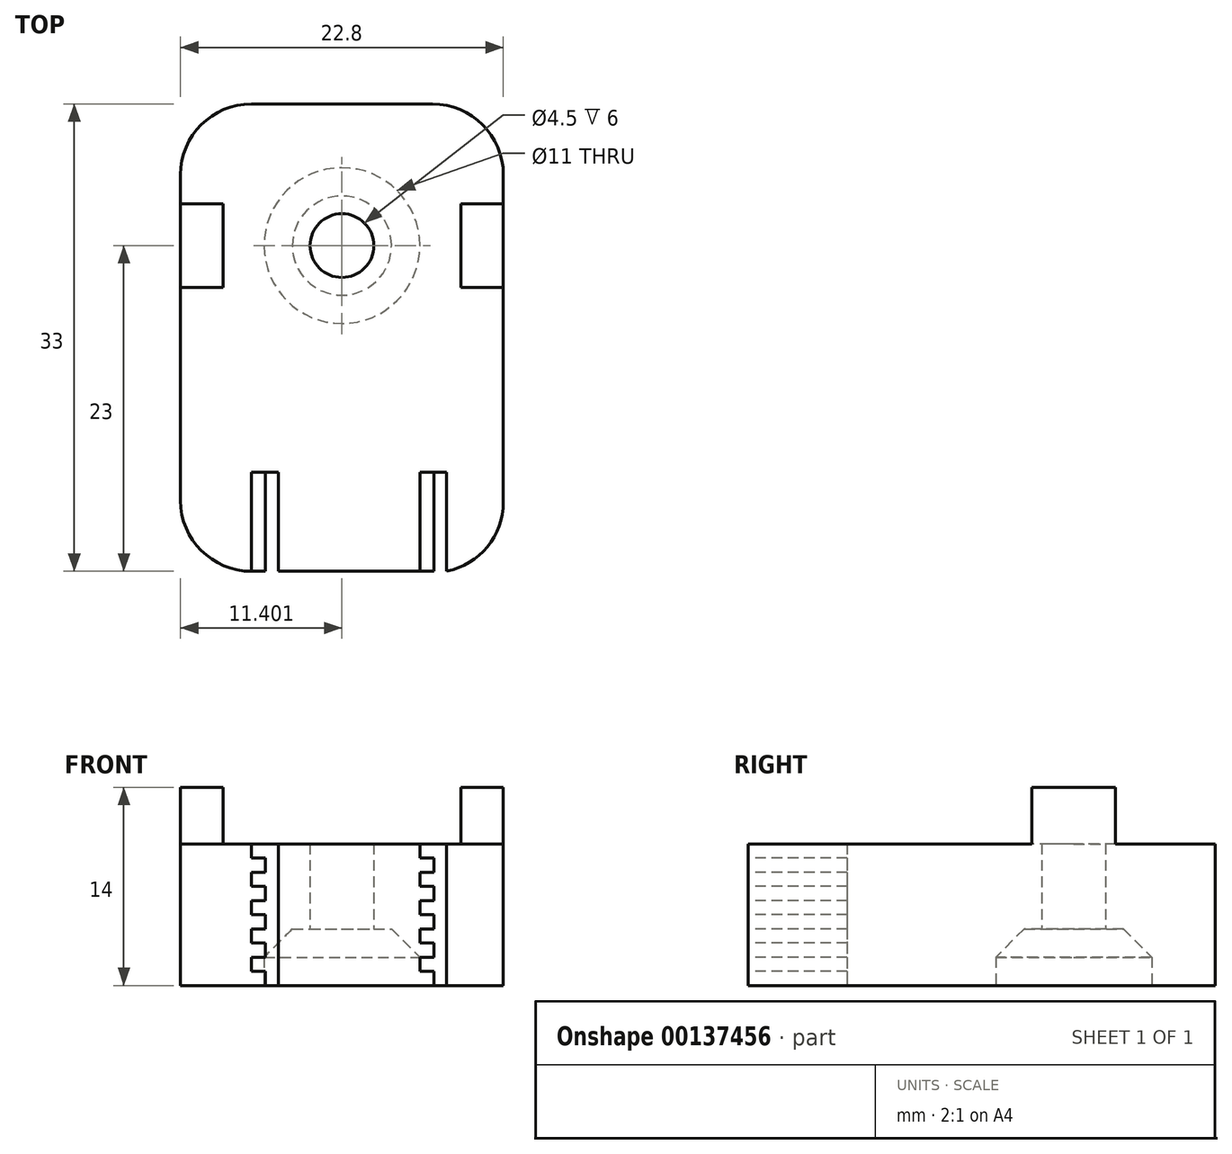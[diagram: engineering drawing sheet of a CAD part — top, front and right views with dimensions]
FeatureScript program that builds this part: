
annotation { "Feature Type Name" : "Feature", "Feature Type Description" : "" }
export const myFeature = defineFeature(function(context is Context, id is Id, definition is map)
    precondition{}
    {
        {
            var Q0;
            Q0=qCreatedBy(makeId("Top.planeOp"),FACE);
            var sketch = newSketch(context, id + "F0", { "sketchPlane" : qUnion([Q0])});
            skLineSegment(sketch, "E0.bottom", {"start": v(-4.06, 0) * mm, "end": v(14.44, 0) * mm});
            skLineSegment(sketch, "E0.top", {"start": v(-4.06, 33) * mm, "end": v(14.44, 33) * mm});
            skLineSegment(sketch, "E0.left", {"start": v(-4.06, 0) * mm, "end": v(-4.06, 33) * mm});
            skLineSegment(sketch, "E0.right", {"start": v(14.44, 0) * mm, "end": v(14.44, 33) * mm});
            skLineSegment(sketch, "E1", {"start": v(-4.06, 13) * mm, "end": v(14.44, 13) * mm});
            skLineSegment(sketch, "E2.bottom", {"start": v(-4.06, 25.95) * mm, "end": v(-1.06, 25.95) * mm});
            skLineSegment(sketch, "E2.top", {"start": v(-4.06, 20.05) * mm, "end": v(-1.06, 20.05) * mm});
            skLineSegment(sketch, "E2.left", {"start": v(-4.06, 25.95) * mm, "end": v(-4.06, 20.05) * mm});
            skLineSegment(sketch, "E2.right", {"start": v(-1.06, 25.95) * mm, "end": v(-1.06, 20.05) * mm});
            skLineSegment(sketch, "E3.bottom", {"start": v(14.44, 25.95) * mm, "end": v(11.44, 25.95) * mm});
            skLineSegment(sketch, "E3.top", {"start": v(14.44, 20.05) * mm, "end": v(11.44, 20.05) * mm});
            skLineSegment(sketch, "E3.left", {"start": v(14.44, 25.95) * mm, "end": v(14.44, 20.05) * mm});
            skLineSegment(sketch, "E3.right", {"start": v(11.44, 25.95) * mm, "end": v(11.44, 20.05) * mm});
            skCircle(sketch, "E4", {"center": v(5.2, 23) * mm, "radius": 2.25 * mm});
            skPoint(sketch, "E5", {"position": v(-1.06, 23) * mm});
            skPoint(sketch, "E6", {"position": v(-4.06, 23) * mm});
            skLineSegment(sketch, "E7", {"start": v(-4.06, 23) * mm, "end": v(14.44, 23) * mm});
            skLineSegment(sketch, "E8.bottom", {"start": v(14.44, 13) * mm, "end": v(18.74, 13) * mm});
            skLineSegment(sketch, "E8.top", {"start": v(14.44, 0) * mm, "end": v(18.74, 0) * mm});
            skLineSegment(sketch, "E8.left", {"start": v(14.44, 13) * mm, "end": v(14.44, 0) * mm});
            skLineSegment(sketch, "E8.right", {"start": v(18.74, 13) * mm, "end": v(18.74, 0) * mm});
            skLineSegment(sketch, "E9.bottom", {"start": v(14.44, 33) * mm, "end": v(18.74, 33) * mm});
            skLineSegment(sketch, "E9.left", {"start": v(14.44, 33) * mm, "end": v(14.44, 13) * mm});
            skLineSegment(sketch, "E9.right", {"start": v(18.74, 33) * mm, "end": v(18.74, 13) * mm});
            skLineSegment(sketch, "E10.bottom", {"start": v(18.74, 25.95) * mm, "end": v(15.74, 25.95) * mm});
            skLineSegment(sketch, "E10.top", {"start": v(18.74, 20.05) * mm, "end": v(15.74, 20.05) * mm});
            skLineSegment(sketch, "E10.left", {"start": v(18.74, 25.95) * mm, "end": v(18.74, 20.05) * mm});
            skLineSegment(sketch, "E10.right", {"start": v(15.74, 25.95) * mm, "end": v(15.74, 20.05) * mm});
            skCircle(sketch, "E11", {"center": v(7.34, 23) * mm, "radius": 2.25 * mm});
            skPoint(sketch, "E12", {"position": v(7.34, 0) * mm});
            skSolve(sketch);
        }
        {
            var Q0;
            {var subQ0=sQuery(id+"F0.wireOp",EDGE,"E0.bottom");Q0=makeQuery(id+"F0.imprint","IMPRINT",FACE,{"disambiguationData":[TD([[makeQuery(id+"F0.imprint","IMPRINT",EDGE,{"derivedFrom":subQ0}),1.0]])]});}
            var Q1;
            Q1=makeQuery(id+"F0.imprint","IMPRINT",FACE,{"disambiguationData":[TD([[makeQuery(id+"F0.imprint","IMPRINT",EDGE,{"derivedFrom":sQuery(id+"F0.wireOp",EDGE,"E8.bottom")}),-1.0]])]});
            var Q2;
            Q2=makeQuery(id+"F0.imprint","IMPRINT",FACE,{"disambiguationData":[TD([[makeQuery(id+"F0.imprint","IMPRINT",EDGE,{"derivedFrom":sQuery(id+"F0.wireOp",EDGE,"E8.top")}),1.0]])]});
            var Q3;
            {var subQ9=sQuery(id+"F0.wireOp",EDGE,"E9.bottom");Q3=makeQuery(id+"F0.imprint","IMPRINT",FACE,{"disambiguationData":[TD([[makeQuery(id+"F0.imprint","IMPRINT",EDGE,{"derivedFrom":subQ9}),-1.0]])]});}
            var Q4;
            {var subQ5=sQuery(id+"F0.wireOp",EDGE,"E1");Q4=makeQuery(id+"F0.imprint","IMPRINT",FACE,{"disambiguationData":[TD([[makeQuery(id+"F0.imprint","IMPRINT",EDGE,{"derivedFrom":subQ5}),1.0]])]});}
            var Q5;
            {var subQ1=sQuery(id+"F0.wireOp",EDGE,"E3.top");Q5=makeQuery(id+"F0.imprint","IMPRINT",FACE,{"disambiguationData":[TD([[makeQuery(id+"F0.imprint","IMPRINT",EDGE,{"derivedFrom":subQ1}),-1.0]])]});}
            var Q6;
            {var subQ6=sQuery(id+"F0.wireOp",EDGE,"E3.bottom");Q6=makeQuery(id+"F0.imprint","IMPRINT",FACE,{"disambiguationData":[TD([[makeQuery(id+"F0.imprint","IMPRINT",EDGE,{"derivedFrom":subQ6}),1.0]])]});}
            var Q7;
            {var subQ5=sQuery(id+"F0.wireOp",EDGE,"E0.top");Q7=makeQuery(id+"F0.imprint","IMPRINT",FACE,{"disambiguationData":[TD([[makeQuery(id+"F0.imprint","IMPRINT",EDGE,{"derivedFrom":subQ5}),-1.0]])]});}
            var Q8;
            {var subQ0=sQuery(id+"F0.wireOp",EDGE,"E7");var subQ1=sQuery(id+"F0.wireOp",EDGE,"E4");var subQ2=makeQuery(id+"F0.imprint","INTERSECT",VERTEX,{"disambiguationData":[OD(1.0)],"derivedFrom":[subQ1,subQ0]});Q8=makeQuery(id+"F0.imprint","IMPRINT",FACE,{"disambiguationData":[TD([[makeQuery(id+"F0.imprint","IMPRINT",EDGE,{"disambiguationData":[TD([[subQ2,-1.0]])],"derivedFrom":subQ1}),1.0]])]});}
            var Q9;
            {var subQ0=sQuery(id+"F0.wireOp",EDGE,"E11");var subQ1=sQuery(id+"F0.wireOp",EDGE,"E4");var subQ2=makeQuery(id+"F0.imprint","INTERSECT",VERTEX,{"disambiguationData":[OD(0.0)],"derivedFrom":[subQ1,subQ0]});Q9=makeQuery(id+"F0.imprint","IMPRINT",FACE,{"disambiguationData":[TD([[makeQuery(id+"F0.imprint","IMPRINT",EDGE,{"disambiguationData":[TD([[subQ2,-1.0]])],"derivedFrom":subQ1}),1.0]])]});}
            extrude(context, id + "F1", {"entities" : qUnion([Q0, Q1, Q2, Q3, Q4, Q5, Q6, Q7, Q8, Q9]), "depth" : 10 * mm});
        }
        {
            var Q0;
            Q0=makeQuery(id+"F1.opExtrude","SWEPT_FACE",FACE,{"disambiguationData":[OSD([sQuery(id+"F0.wireOp",EDGE,"E0.bottom")])]});
            var sketch = newSketch(context, id + "F2", { "sketchPlane" : qUnion([Q0])});
            skLineSegment(sketch, "E13", {"start": v(0.94, 10) * mm, "end": v(0.94, 9) * mm});
            skLineSegment(sketch, "E14", {"start": v(0.94, 9) * mm, "end": v(1.94, 9) * mm});
            skLineSegment(sketch, "E15", {"start": v(1.94, 9) * mm, "end": v(1.94, 8) * mm});
            skLineSegment(sketch, "E16", {"start": v(1.94, 8) * mm, "end": v(0.94, 8) * mm});
            skLineSegment(sketch, "E17", {"start": v(0.94, 8) * mm, "end": v(0.94, 7) * mm});
            skLineSegment(sketch, "E18", {"start": v(0.94, 7) * mm, "end": v(1.94, 7) * mm});
            skLineSegment(sketch, "E19", {"start": v(1.94, 7) * mm, "end": v(1.94, 6) * mm});
            skLineSegment(sketch, "E20", {"start": v(1.94, 6) * mm, "end": v(0.94, 6) * mm});
            skLineSegment(sketch, "E21", {"start": v(0.94, 6) * mm, "end": v(0.94, 5) * mm});
            skLineSegment(sketch, "E22", {"start": v(0.94, 5) * mm, "end": v(1.94, 5) * mm});
            skLineSegment(sketch, "E23", {"start": v(1.94, 5) * mm, "end": v(1.94, 4) * mm});
            skLineSegment(sketch, "E24", {"start": v(1.94, 4) * mm, "end": v(0.94, 4) * mm});
            skLineSegment(sketch, "E25", {"start": v(0.94, 4) * mm, "end": v(0.94, 3) * mm});
            skLineSegment(sketch, "E26", {"start": v(0.94, 3) * mm, "end": v(1.94, 3) * mm});
            skLineSegment(sketch, "E27", {"start": v(1.94, 3) * mm, "end": v(1.94, 2) * mm});
            skLineSegment(sketch, "E28", {"start": v(1.94, 2) * mm, "end": v(0.94, 2) * mm});
            skLineSegment(sketch, "E29", {"start": v(0.94, 2) * mm, "end": v(0.94, 1) * mm});
            skLineSegment(sketch, "E30", {"start": v(0.94, 1) * mm, "end": v(1.94, 1) * mm});
            skLineSegment(sketch, "E31", {"start": v(1.94, 1) * mm, "end": v(1.94, 0) * mm});
            skLineSegment(sketch, "E32", {"start": v(1.94, 0) * mm, "end": v(0.94, 0) * mm});
            skLineSegment(sketch, "E33", {"start": v(2.84, 10) * mm, "end": v(2.84, 0) * mm});
            skLineSegment(sketch, "E34", {"start": v(0.94, 10) * mm, "end": v(2.84, 10) * mm});
            skLineSegment(sketch, "E35", {"start": v(2.84, 0) * mm, "end": v(1.94, 0) * mm});
            skLineSegment(sketch, "E36", {"start": v(12.84, 10) * mm, "end": v(12.84, 9) * mm});
            skLineSegment(sketch, "E37", {"start": v(12.84, 9) * mm, "end": v(13.84, 9) * mm});
            skLineSegment(sketch, "E38", {"start": v(13.84, 9) * mm, "end": v(13.84, 8) * mm});
            skLineSegment(sketch, "E39", {"start": v(13.84, 8) * mm, "end": v(12.84, 8) * mm});
            skLineSegment(sketch, "E40", {"start": v(12.84, 8) * mm, "end": v(12.84, 7) * mm});
            skLineSegment(sketch, "E41", {"start": v(12.84, 7) * mm, "end": v(13.84, 7) * mm});
            skLineSegment(sketch, "E42", {"start": v(13.84, 7) * mm, "end": v(13.84, 6) * mm});
            skLineSegment(sketch, "E43", {"start": v(13.84, 6) * mm, "end": v(12.84, 6) * mm});
            skLineSegment(sketch, "E44", {"start": v(12.84, 6) * mm, "end": v(12.84, 5) * mm});
            skLineSegment(sketch, "E45", {"start": v(12.84, 5) * mm, "end": v(13.84, 5) * mm});
            skLineSegment(sketch, "E46", {"start": v(13.84, 5) * mm, "end": v(13.84, 4) * mm});
            skLineSegment(sketch, "E47", {"start": v(13.84, 4) * mm, "end": v(12.84, 4) * mm});
            skLineSegment(sketch, "E48", {"start": v(12.84, 4) * mm, "end": v(12.84, 3) * mm});
            skLineSegment(sketch, "E49", {"start": v(12.84, 3) * mm, "end": v(13.84, 3) * mm});
            skLineSegment(sketch, "E50", {"start": v(13.84, 3) * mm, "end": v(13.84, 2) * mm});
            skLineSegment(sketch, "E51", {"start": v(13.84, 2) * mm, "end": v(12.84, 2) * mm});
            skLineSegment(sketch, "E52", {"start": v(12.84, 2) * mm, "end": v(12.84, 1) * mm});
            skLineSegment(sketch, "E53", {"start": v(12.84, 1) * mm, "end": v(13.84, 1) * mm});
            skLineSegment(sketch, "E54", {"start": v(13.84, 1) * mm, "end": v(13.84, 0) * mm});
            skLineSegment(sketch, "E55", {"start": v(13.84, 0) * mm, "end": v(12.84, 0) * mm});
            skLineSegment(sketch, "E56", {"start": v(14.74, 10) * mm, "end": v(14.74, 0) * mm});
            skLineSegment(sketch, "E57", {"start": v(12.84, 10) * mm, "end": v(14.74, 10) * mm});
            skLineSegment(sketch, "E58", {"start": v(14.74, 0) * mm, "end": v(13.84, 0) * mm});
            skPoint(sketch, "E59.centerSnap0", {"position": v(-4.06, 5) * mm});
            skPoint(sketch, "E60", {"position": v(7.34, 10) * mm});
            skSolve(sketch);
        }
        {
            var Q0;
            Q0=makeQuery(id+"F2.imprint","IMPRINT",FACE,{"disambiguationData":[TD([[makeQuery(id+"F2.imprint","IMPRINT",EDGE,{"derivedFrom":sQuery(id+"F2.wireOp",EDGE,"E13")}),1.0]])]});
            var Q1;
            Q1=makeQuery(id+"F2.imprint","IMPRINT",FACE,{"disambiguationData":[TD([[makeQuery(id+"F2.imprint","IMPRINT",EDGE,{"derivedFrom":sQuery(id+"F2.wireOp",EDGE,"E36")}),1.0]])]});
            extrude(context, id + "F3", {"entities" : qUnion([Q0, Q1]), "operationType" : NewBodyOperationType.REMOVE, "oppositeDirection" : true, "depth" : 7 * mm});
        }
        {
            var Q0;
            Q0=makeQuery(id+"F1.opExtrude","SWEPT_EDGE",EDGE,{"disambiguationData":[OSD([sQuery(id+"F0.wireOp",EDGE,"E0.top"),sQuery(id+"F0.wireOp",EDGE,"E0.right")])]});
            var Q1;
            Q1=makeQuery(id+"F1.opExtrude","SWEPT_EDGE",EDGE,{"disambiguationData":[OSD([sQuery(id+"F0.wireOp",EDGE,"E0.top"),sQuery(id+"F0.wireOp",EDGE,"E0.left")])]});
            var Q2;
            Q2=makeQuery(id+"F1.opExtrude","SWEPT_EDGE",EDGE,{"disambiguationData":[OSD([sQuery(id+"F0.wireOp",EDGE,"E0.bottom"),sQuery(id+"F0.wireOp",EDGE,"E0.left")])]});
            var Q3;
            Q3=makeQuery(id+"F1.opExtrude","SWEPT_EDGE",EDGE,{"disambiguationData":[OSD([sQuery(id+"F0.wireOp",EDGE,"E0.bottom"),sQuery(id+"F0.wireOp",EDGE,"E0.right")])]});
            var Q4;
            Q4=makeQuery(id+"F1.opExtrude","SWEPT_EDGE",EDGE,{"disambiguationData":[OSD([sQuery(id+"F0.wireOp",EDGE,"E8.top"),sQuery(id+"F0.wireOp",EDGE,"E8.right")])]});
            var Q5;
            Q5=makeQuery(id+"F1.opExtrude","SWEPT_EDGE",EDGE,{"disambiguationData":[OSD([sQuery(id+"F0.wireOp",EDGE,"E8.bottom"),sQuery(id+"F0.wireOp",EDGE,"E8.right")])]});
            var Q6;
            Q6=makeQuery(id+"F1.opExtrude","SWEPT_EDGE",EDGE,{"disambiguationData":[OSD([sQuery(id+"F0.wireOp",EDGE,"E9.bottom"),sQuery(id+"F0.wireOp",EDGE,"E9.right")])]});
            fillet(context, id + "F4", {"entities" : qUnion([Q0, Q1, Q2, Q3, Q4, Q5, Q6]), "radius" : 5 * mm, "tangentPropagation" : true, "allowEdgeOverflow" : false});
        }
        {
            var Q0;
            {var subQ0=sQuery(id+"F0.wireOp",EDGE,"E2.bottom");Q0=makeQuery(id+"F0.imprint","IMPRINT",FACE,{"disambiguationData":[TD([[makeQuery(id+"F0.imprint","IMPRINT",EDGE,{"derivedFrom":subQ0}),-1.0]])]});}
            var Q1;
            {var subQ0=sQuery(id+"F0.wireOp",EDGE,"E2.top");Q1=makeQuery(id+"F0.imprint","IMPRINT",FACE,{"disambiguationData":[TD([[makeQuery(id+"F0.imprint","IMPRINT",EDGE,{"derivedFrom":subQ0}),1.0]])]});}
            var Q2;
            Q2=makeQuery(id+"F0.imprint","IMPRINT",FACE,{"disambiguationData":[TD([[makeQuery(id+"F0.imprint","IMPRINT",EDGE,{"derivedFrom":sQuery(id+"F0.wireOp",EDGE,"E10.bottom")}),1.0]])]});
            extrude(context, id + "F5", {"entities" : qUnion([Q0, Q1, Q2]), "operationType" : NewBodyOperationType.ADD, "depth" : 14 * mm});
        }
        {
            var Q0;
            {var subQ0=sQuery(id+"F0.wireOp",EDGE,"E10.right");var subQ1=sQuery(id+"F0.wireOp",EDGE,"E10.top");var subQ2=sQuery(id+"F0.wireOp",EDGE,"E10.bottom");var subQ3=sQuery(id+"F0.wireOp",EDGE,"E2.right");var subQ4=sQuery(id+"F0.wireOp",EDGE,"E2.top");var subQ5=sQuery(id+"F0.wireOp",EDGE,"E2.bottom");Q0=makeQuery(id+"F5.boolean.opBoolean","MERGE",FACE,{"derivedFrom":[makeQuery(id+"F1.opExtrude","CAP_FACE",FACE,{"disambiguationData":[OSD([sQuery(id+"F0.wireOp",EDGE,"E0.bottom"),sQuery(id+"F0.wireOp",EDGE,"E0.top"),sQuery(id+"F0.wireOp",EDGE,"E0.left"),subQ5,subQ4,subQ3,sQuery(id+"F0.wireOp",EDGE,"E8.top"),sQuery(id+"F0.wireOp",EDGE,"E8.right"),sQuery(id+"F0.wireOp",EDGE,"E9.bottom"),sQuery(id+"F0.wireOp",EDGE,"E9.right"),subQ2,subQ1,subQ0,sQuery(id+"F0.wireOp",EDGE,"E11")])],"isStart":true}),makeQuery(id+"F5.opExtrude","CAP_FACE",FACE,{"disambiguationData":[OSD([subQ5,subQ4,sQuery(id+"F0.wireOp",EDGE,"E2.left"),subQ3])],"isStart":true}),makeQuery(id+"F5.opExtrude","CAP_FACE",FACE,{"disambiguationData":[OSD([subQ2,subQ1,sQuery(id+"F0.wireOp",EDGE,"E10.left"),subQ0])],"isStart":true})]});}
            var sketch = newSketch(context, id + "F6", { "sketchPlane" : qUnion([Q0])});
            skCircle(sketch, "E61", {"center": v(7.34, -23) * mm, "radius": 5.5 * mm});
            skSolve(sketch);
        }
        {
            var Q0;
            Q0=qSketchRegion(id+"F6",true);
            extrude(context, id + "F7", {"entities" : qUnion([Q0]), "operationType" : NewBodyOperationType.REMOVE, "oppositeDirection" : true, "depth" : 4 * mm});
        }
        {
            var Q0;
            Q0=makeQuery(id+"F7.boolean.opBoolean","COPY",EDGE,{"derivedFrom":makeQuery(id+"F7.opExtrude","CAP_EDGE",EDGE,{"disambiguationData":[OSD([sQuery(id+"F6.wireOp",EDGE,"E61")])],"isStart":false})});
            chamfer(context, id + "F8", {"entities" : qUnion([Q0]), "width" : 2 * mm, "tangentPropagation" : true});
        }
    });
